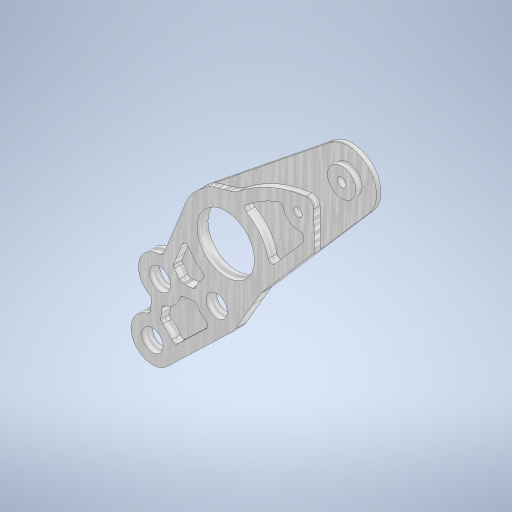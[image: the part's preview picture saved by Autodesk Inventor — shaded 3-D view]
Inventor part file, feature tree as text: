
AUTODESK INVENTOR PART (.ipt)
format: ipt  version: 2023.1 (Build 271208000, 208)  size: 1,289,728 bytes
history: native  units: mm
features: projected_geometry x24, extrude x23, sketch x23, other x8, fillet x7, shell x1, reference x1
ambient origin geometry x8: Origin, YZ Plane, XZ Plane, XY Plane, X Axis, Y Axis, Z Axis, Center Point
bodies: Body1 (feature_tree)
feature tree (87):
  other  "ソリッド1"
  extrude  "押し出し1"  Depth=17.05mm
  extrude  "押し出し3"  Depth=2.5mm
  extrude  "押し出し4"  Depth=3.0mm TaperAngle=0.0deg
  fillet  "フィレット1"  Radius=8.0mm
  extrude  "押し出し5"  Depth=2.5mm
  sketch  "スケッチ6"
  shell  "シェル2"  Thickness=2.0mm
  fillet  "フィレット2"  Radius=0.5mm
  extrude  "押し出し6"  Depth=2.0mm TaperAngle=0.0deg
  sketch  "スケッチ10"
  sketch  "スケッチ11"
  sketch  "スケッチ12"
  sketch  "スケッチ13"
  extrude  "押し出し7"  Depth=2.0mm
  extrude  "押し出し8"  Depth=9.0mm
  extrude  "押し出し9"  Depth=2.5mm
  extrude  "押し出し10"  TaperAngle=0.0deg  [1 undecoded]
  extrude  "押し出し11"  Depth=3.1mm
  sketch  "スケッチ15"
  extrude  "押し出し12"  Depth=3.1mm
  extrude  "押し出し13"  Depth=3.1mm
  fillet  "フィレット3"  Radius=3.1mm
  extrude  "押し出し14"  Depth=3.1mm
  extrude  "押し出し15"  Depth=3.0mm
  extrude  "押し出し16"  Depth=1.0mm
  fillet  "フィレット4"  Radius=0.5mm
  sketch  "スケッチ19"
  extrude  "押し出し17"  Depth=0.3mm
  extrude  "押し出し18"  Depth=1.0mm
  extrude  "押し出し19"  Depth=25.05mm
  sketch  "スケッチ20"
  extrude  "押し出し20"  Depth=6.0mm
  extrude  "押し出し21"  Depth=6.0mm
  fillet  "フィレット5"  Radius=6.0mm
  sketch  "スケッチ23"
  extrude  "押し出し22"  Depth=12.0mm
  extrude  "押し出し23"  Depth=12.0mm
  fillet  "フィレット6"  Radius=12.0mm
  fillet  "フィレット7"  Radius=3.0mm
  sketch  "スケッチ24"
  sketch  "スケッチ25"
  extrude  "押し出し24"  Depth=3.0mm
  sketch  "スケッチ1"
  sketch  "スケッチ3"
  sketch  "スケッチ4"
  reference  "参照1"
  projected_geometry  "投影ループ1"
  projected_geometry  "投影ループ2"
  sketch  "スケッチ5"
  projected_geometry  "投影ループ3"
  projected_geometry  "投影ループ4"
  sketch  "スケッチ9"
  projected_geometry  "投影ループ6"
  projected_geometry  "投影ループ8"
  projected_geometry  "投影ループ9"
  projected_geometry  "投影ループ10"
  projected_geometry  "投影ループ11"
  sketch  "スケッチ14"
  projected_geometry  "投影ループ12"
  projected_geometry  "投影ループ13"
  sketch  "スケッチ16"
  projected_geometry  "投影ループ14"
  sketch  "スケッチ17"
  projected_geometry  "投影ループ15"
  sketch  "スケッチ18"
  projected_geometry  "投影ループ16"
  projected_geometry  "投影ループ17"
  projected_geometry  "投影ループ18"
  sketch  "スケッチ21"
  projected_geometry  "投影ループ19"
  sketch  "スケッチ22"
  projected_geometry  "投影ループ20"
  projected_geometry  "投影ループ21"
  projected_geometry  "投影ループ22"
  projected_geometry  "投影ループ23"
  projected_geometry  "投影ループ24"
  projected_geometry  "投影ループ25"
  sketch  "スケッチ26"
  projected_geometry  "投影ループ26"
  other  "<userpath>\Desktop\院2年機大型\アーム アームユニットアセンブリ.iam"
  other  "アーム アームユニットアセンブリ.iam"
  other  "アーム揺動節2:1"
  other  "断面エッジを投影1"
  other  "断面エッジを投影2"
  other  "断面エッジを投影3"
  other  "断面エッジを投影4"
note: 1 required parameter value undecoded (feature->parameter linkage not recoverable at this tier; creation-order binding heuristic only, values carry confidence <= 0.55)
